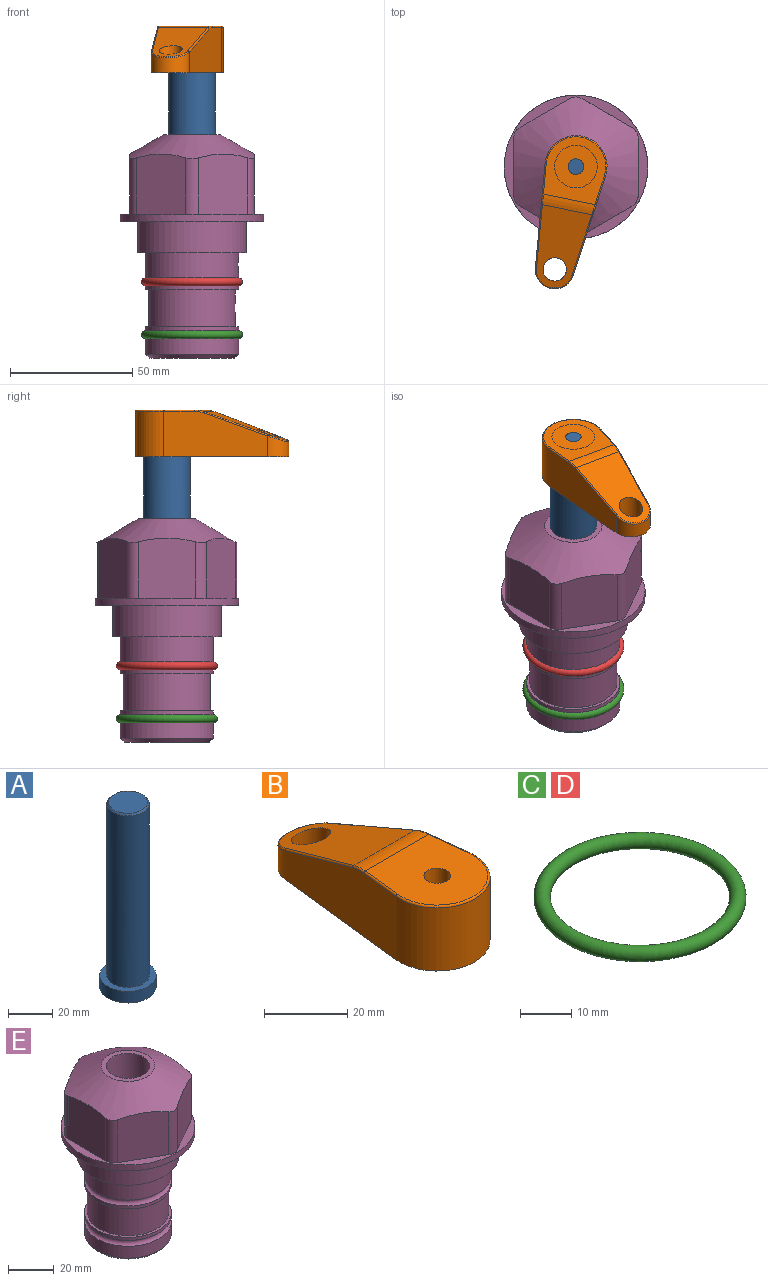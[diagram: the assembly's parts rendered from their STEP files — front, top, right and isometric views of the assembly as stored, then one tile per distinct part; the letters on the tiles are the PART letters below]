
ASSEMBLY  parts=5 mates=3
PART A: 6 faces, bbox 25.4x25.4x101.6 mm
  f0: plane 17.46x17.46mm, normal (0,0,1), area 239.5mm2, adj f5
  f1: plane 25.4x25.4mm, normal (0,0,-1), area 506.7mm2, adj f2
  f2: cylinder r=12.7mm len=25.4mm, axis (0,0,1), area 506.7mm2, adj f1,f3
  f3: plane 25.4x25.4mm, normal (0,0,1), area 221.7mm2, adj f2,f4
  f4: cylinder r=9.53mm len=94.46mm, axis (0,0,1), area 5653mm2, adj f3,f5
  f5: cone r=8.73mm half-angle=45deg, axis (0,0,-1), area 64.4mm2, adj f0,f4
PART B: 29 faces, bbox 27.5x64.6x19.1 mm
  f0: plane 12.7x12.7mm, normal (0,0,-1), area 95mm2, adj f6,f22
  f1: plane 63.5x25.4mm, normal (0,0,-1), area 490.5mm2, adj f2,f3,f4,f5,f7,f19,f20,f21
  f2: cylinder r=12.7mm len=25.4mm, axis (0,0,-1), area 792.2mm2, adj f1,f3,f5,f13
  f3: plane 42.33x18.54mm, normal (0.99,0.11,0), area 647mm2, adj f1,f2,f4,f11,f12,f14
  f4: cylinder r=7.94mm len=15.78mm, axis (0,0,-1), area 158.6mm2, adj f1,f3,f5,f16
  f5: plane 42.33x18.54mm, normal (-0.99,0.11,0), area 647mm2, adj f1,f2,f4,f15,f17,f18
  f6: cylinder r=3.17mm len=19.05mm, axis (0,0,-1), area 380mm2, adj f0,f8
  f7: cylinder r=4.76mm len=10.98mm, axis (0,0,-1), area 276.1mm2, adj f1,f9
  f8: plane 25.83x24.38mm, normal (0,0,1), area 515.5mm2, adj f6,f10,f11,f13,f15
  f9: plane 32.49x20.55mm, normal (0,0.34,0.94), area 489.9mm2, adj f7,f10,f14,f16,f18
  f10: cylinder r=12.7mm len=21.49mm, axis (-1,0,0), area 93.2mm2, adj f8,f9,f12,f17
  f11: cylinder r=0.51mm len=12.34mm, axis (0.11,-0.99,0), area 9.9mm2, adj f3,f8,f12,f13
  f12: bspline ~7.62x1.64mm, area 3.5mm2, adj f3,f10,f11,f14
  f13: torus R=12.19mm, axis (0,0,1), area 33.6mm2, adj f2,f8,f11,f15
  f14: cylinder r=0.51mm len=26.01mm, axis (0.1,-0.93,0.34), area 21.6mm2, adj f3,f9,f12,f16
  f15: cylinder r=0.51mm len=12.34mm, axis (0.11,0.99,0), area 9.9mm2, adj f5,f8,f13,f17
  f16: bspline ~15.78x7.05mm, area 15.7mm2, adj f4,f9,f14,f18
  f17: bspline ~7.62x1.64mm, area 3.5mm2, adj f5,f10,f15,f18
  f18: cylinder r=0.51mm len=26.01mm, axis (0.1,0.93,-0.34), area 21.6mm2, adj f5,f9,f16,f17
  f19: cylinder r=9.53mm len=19.05mm, axis (0,0,-1), area 508.7mm2, adj f1,f20,f21,f24
  f20: plane 33.41x15.88mm, normal (-0.99,-0.11,0), area 466.3mm2, adj f1,f19,f24,f25,f26,f27
  f21: plane 33.41x15.88mm, normal (0.99,-0.11,0), area 466.3mm2, adj f1,f19,f24,f25,f26,f28
  f22: cylinder r=6.35mm len=15.88mm, axis (0,0,-1), area 633.4mm2, adj f0,f24
  f23: cylinder r=7.94mm len=8.74mm, axis (0,0,-1), area 61.9mm2, adj f1,f25,f27,f28
  f24: plane 23.16x19.05mm, normal (0,0,-1), area 256.4mm2, adj f19,f20,f21,f22,f26
  f25: plane 18.98x15.39mm, normal (0,-0.34,-0.94), area 262mm2, adj f20,f21,f23,f26,f27,f28
  f26: cylinder r=9.53mm len=16.12mm, axis (-1,0,0), area 52.4mm2, adj f20,f21,f24,f25
  f27: cylinder r=1.59mm len=8.9mm, axis (0,0,-1), area 25.9mm2, adj f1,f20,f23,f25
  f28: cylinder r=1.59mm len=8.9mm, axis (0,0,-1), area 25.9mm2, adj f1,f21,f23,f25
PART C: 1 faces, bbox 44.7x44.7x3.2 mm
  f0: torus R=19.05mm, axis (0,0,1), area 1193.9mm2
PART D: same geometry as C
PART E: 36 faces, bbox 58.7x58.7x91.2 mm
  f0: cylinder r=17.78mm len=35.56mm, axis (0,0,1), area 1670.8mm2, adj f23,f24,f31
  f1: cylinder r=19.05mm len=38.1mm, axis (0,0,1), area 1191.9mm2, adj f26,f27,f30
  f2: plane 58.66x58.66mm, normal (0,0,-1), area 1150.6mm2, adj f3,f28
  f3: cylinder r=29.33mm len=58.66mm, axis (0,0,-1), area 585.1mm2, adj f2,f4
  f4: plane 58.66x58.66mm, normal (0,0,1), area 475.9mm2, adj f3,f5,f6,f7,f8,f9,f10,f11
  f5: plane 24.5x20.32mm, normal (-0.5,0.87,0), area 562.8mm2, adj f4,f15,f16,f17
  f6: plane 24.5x20.32mm, normal (0.5,0.87,0), area 562.8mm2, adj f4,f14,f15,f17
  f7: plane 24.5x23.48mm, normal (1,0,0), area 562.8mm2, adj f4,f13,f14,f17
  f8: plane 24.5x20.32mm, normal (0.5,-0.87,0), area 562.8mm2, adj f4,f12,f13,f17
  f9: plane 24.5x20.32mm, normal (-0.5,-0.87,0), area 562.8mm2, adj f4,f11,f12,f17
  f10: plane 24.5x23.48mm, normal (-1,0,0), area 562.8mm2, adj f4,f11,f16,f17
  f11: cylinder r=5.08mm len=23.01mm, axis (0,0,-1), area 121.2mm2, adj f4,f9,f10,f17
  f12: cylinder r=5.08mm len=23.01mm, axis (0,0,-1), area 121.2mm2, adj f4,f8,f9,f17
  f13: cylinder r=5.08mm len=23.01mm, axis (0,0,-1), area 121.2mm2, adj f4,f7,f8,f17
  f14: cylinder r=5.08mm len=23.01mm, axis (0,0,-1), area 121.2mm2, adj f4,f6,f7,f17
  f15: cylinder r=5.08mm len=23.01mm, axis (0,0,-1), area 121.2mm2, adj f4,f5,f6,f17
  f16: cylinder r=5.08mm len=23.01mm, axis (0,0,-1), area 121.2mm2, adj f4,f5,f10,f17
  f17: cone r=11.73mm half-angle=60deg, axis (0,0,-1), area 2071.8mm2, adj f5,f6,f7,f8,f9,f10,f11,f12
  f18: plane 23.46x23.46mm, normal (0,0,1), area 147.4mm2, adj f17,f35
  f19: plane 34.93x34.93mm, normal (0,0,-1), area 958mm2, adj f29
  f20: cylinder r=19.05mm len=38.1mm, axis (0,0,1), area 760.1mm2, adj f21,f29
  f21: torus R=19.05mm, axis (0,0,1), area 565.3mm2, adj f20,f22
  f22: cylinder r=19.05mm len=38.1mm, axis (0,0,1), area 190mm2, adj f21,f23
  f23: plane 38.1x38.1mm, normal (0,0,1), area 146.9mm2, adj f0,f22
  f24: plane 38.1x38.1mm, normal (0,0,-1), area 146.9mm2, adj f0,f25
  f25: cylinder r=19.05mm len=38.1mm, axis (0,0,1), area 190mm2, adj f24,f26
  f26: torus R=19.05mm, axis (0,0,1), area 565.3mm2, adj f1,f25
  f27: plane 44.45x44.45mm, normal (0,0,-1), area 411.7mm2, adj f1,f28
  f28: cylinder r=22.23mm len=44.45mm, axis (0,0,1), area 1773.5mm2, adj f2,f27
  f29: cone r=19.05mm half-angle=45deg, axis (0,0,1), area 257.5mm2, adj f19,f20
  f30: cylinder r=3.17mm len=6.75mm, axis (-1,0,0), area 128mm2, adj f1,f33
  f31: cylinder r=3.17mm len=6.35mm, axis (-1,0,0), area 102.5mm2, adj f0,f33
  f32: plane 25.4x25.4mm, normal (0,0,1), area 506.7mm2, adj f33
  f33: cylinder r=12.7mm len=66.42mm, axis (0,0,-1), area 5236.2mm2, adj f30,f31,f32,f34
  f34: cone r=9.53mm half-angle=30deg, axis (0,0,-1), area 443.4mm2, adj f33,f35
  f35: cylinder r=9.53mm len=19.05mm, axis (0,0,-1), area 849mm2, adj f18,f34
PLACE A rot(axis=(0,0,-1),101.7deg) t=(0,0,6.38)mm
PLACE B rot(axis=(0,0,1),168.3deg) t=(0,0,60.99)mm
PLACE C t=(0,0,-21.59)mm
PLACE D at identity
PLACE E at identity fixed
MATE fastened C.f0 <-> E.f0  axis (0,0,1) through (0,0,-46.1)mm
MATE cylindrical A.f2 <-> E.f0  axis (0,0,1) through (0,0,32.01)mm
MATE fastened B.f2 <-> A.f2  axis (0,0,1) through (0,0,80.04)mm
